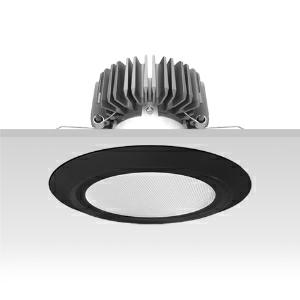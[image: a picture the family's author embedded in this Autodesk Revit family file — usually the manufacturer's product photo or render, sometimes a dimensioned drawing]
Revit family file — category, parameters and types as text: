
# Revit family: 3f_filippi_-_3f_reno_bianco_ampio_3f_filippi_-_30679_a01038_-_3f_reno_200_wh_3000-840_dali_wide___vs_bk_3861
name_source: partatom
category: Lighting Fixtures
units: mm (PartAtom-declared; Revit-internal decimal feet)

## family parameters
Cut with Voids When Loaded = No
Host = Face
Light Source = No
Part Type = Normal
Room Calculation Point = No
Round Connector Dimension = Use Diameter
Shared = No

## types (1)
- 3F Filippi - 3F Reno Bianco Ampio (1 x LED, 2312 lm, 28 W, 4000 K)
    Apparent Load = 28 VA
    Approval mark = CE
    CIE Flux Codes = 75 94 99 100 100
    Color Rendering = 80
    Color Temperature = 4000 K
    Control Gear = Electronic transformer
    Default Elevation = 1800 mm
    Description = ILLUMINOTECHNICAL
Luminous efficiency 100% (DLOR 100%, ULOR 0%).
Initial luminous flux of the luminaire 2312 lm.
Direct symmetric wide distribution.
Installation Interdistance Transv.D = 1.16 x hu - Long.D = 1.14 x hu.
Tabular UGR (CIE 117 - 4H-8H; S=0.25H; 70/50/20): RUG 21.5 - 21.4.
Beam angle: 74° - 74°.
Luminous efficacy 83 lm/W.
Lifetime (L90/B10): 30000 h. (tq+25°C)
Lifetime (L85/B10): 50000 h. (tq+25°C)
Lifetime (L70/B10): 80000 h. (tq+25°C)
Sudden decreased luminous flux after 50000 hours: 0% (C0).
Photobiological safety in compliance with IEC/TR 62778: RG0 risk exempt, (IEC 62471).
In compliance with IEC/EN 62722-2-1 - IEC/EN 62717 standards.

SOURCE
Compact LED module 3000/840.
Energy efficiency class (UE 2019/2020 - UE 2019/2015): E.
CIE 13.3 Colour rendering index: CRI >80 (R9 <50%).
IES TM-30 Fidelity Index: Rf = 84 Rg = 95.
CCT nominal colour temperature 4000 K.
Colour initial tolerance (MacAdam): SDCM 3.
Zhaga Book 3 compliant.

MECHANICAL
Passive heat dissipator in die-casting aluminium, oversized, for optimum thermal management of the LED module.
Parabolic element with graduated/concentric rings in white polycarbonate.
Transparent external lens with glossy and satin differentiated surfaces, with a cooling and anti-insect system in methacrylate (PMMA).
Fastening spring clips in stainless steel.
Dimensions: diameter 226 mm, height 146 mm. Weight 1.825 kg.
IP44 protection degree for exposed part, IP20 for recessed part.
Mechanical strength to impacts IK06 (1 joule).
Glow-wire test resistance 650°C.

ELECTRICAL
Wiring on a separate unit.
Halogen Free DALI-2 DATI (Parts 251, 252, 253), PUSH-DIM, electronic wiring 230V-50/60Hz, power factor 0.97 at full load, THD <25%, constant output current, SELV, class II, 1 driver, 1 DALI addresse.
Power of the luminaire 28 W.
ENEC - CE.
SAFE FLICKER: PstLM=<1 and SVM=<0.4 (IEC TR 61547-1 and IEC TR 63158), to ensure a more comfortable and safe light.
Luminaire compliant with EN 60598-2-22 for power supply from a centralised emergency system CPSS (Central Power Supply System), not incorporated in the luminaire - high risk areas excluded. The default power and flux are 100% in AC and 100% in DC.
Ambient temperature from 0°C to +25°C.
Temperature class T6 max 85°C.
Relative humidity UR: <85%.

INSTALLATION
Pull-up recessed fitting.
False ceiling carving: 200 mm.
All accessories dedicated to this product are available on the Catalog and on our website www.3F-Filippi.com.

ACCESSORIES
A01038 - Anti-glare microprismatic VS moulded glass, tempered, not flammable, locked and in line with the trim, in black polycarbonate.

APPLICATIONS
Environments: architectural, commercial, exhibition areas, transit areas, corridors, shops, display windows, service areas.
In false ceilings with narrow voids.

LIGHT MANAGEMENT
Recommended minimum setting: 10%.
The luminaire, equipped with (DALI-2 DATI) driver, can be controlled manually with 3F Easy Dim technology or automatically/manually with wired or wireless DALI/D2D control systems.
The D2D driver guarantees interoperability with other devices with the same certification by making the following information available:
Device Data (Part 251), Energy Report (Part 252), Diagnosis & Maintenance (Part 253).
In electrical systems without a regulation system (manual or automatic) and DALI bus, a suitable jumper must be made on the DA-DA terminals of the appliance.

WARNING
Luminaire designed for disposal/recycling at end-of-life.
Replaceable (LED only) light source by a professional. Replaceable control gear by a professional.
    Height = 0 mm  [stored 0 ft]
    Lamp = 1 x LED
    Lamp Light Flux = 2312 lm
    Lamp Power = 28 W
    Lamp count = 1
    Length = 226 mm
    Lifetime = 50000 h
    Luminous efficacy = 83 lm/W
    Manufacturer = 3F Filippi
    ModVariant = No
    Model = 3F Filippi - 30679+A01038 - 3F Reno 200 WH 3000-840 DALI WIDE + VS BK
    Mounting Place = Ceiling
    Mounting Type = Recessed
    Number of Poles = 1
    OnlyDefault = Yes
    Power Factor = 1
    Product Name = 3F Filippi - 3F Reno Bianco Ampio
    Product group = recessed luminaire
    ProductGroupID = 4
    Protection Class = Protection class II
    Protection Degree = IP 20
    RLX_Detail_Level = 1
    RLX_Emergency_Light_Flux = 0 lm
    RLX_Emergency_Type = 0
    RLX_Emergency_Type_DB = No
    RlxData = <blob elided: 99461 chars, md5=98ea6bff>
    Socket = socket
    Standby Power = 0 W
    System Light Flux = 2312 lm
    System Power = 28 W
    Type Comments = Product without accessories
    Type Image = 3ffilippi_3f_reno_200_bk_vs_smp.jpg
    URL = http://relux.com
    VarID = ---
    Voltage = 0 V
    Weight = 0.00 kg
    Width = 0 mm  [stored 0 ft]

note: [stored X ft] marks values corroborated as IEEE doubles in the binary element streams (Revit-internal decimal feet)

## geometry (parser evidence)
native form markers: Blend x4, Sweep x11
no freeform markers — native parametric forms only
